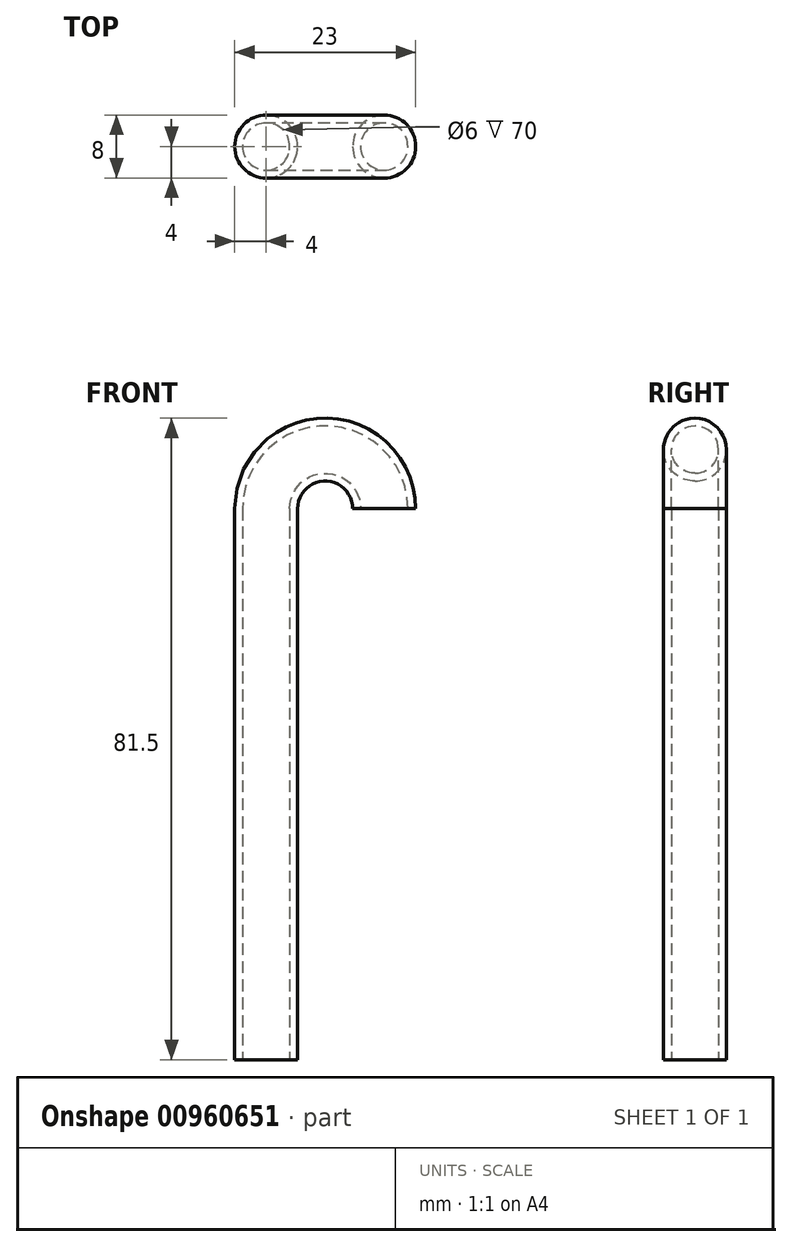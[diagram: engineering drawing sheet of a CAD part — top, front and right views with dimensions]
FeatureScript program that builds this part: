
annotation { "Feature Type Name" : "Feature", "Feature Type Description" : "" }
export const myFeature = defineFeature(function(context is Context, id is Id, definition is map)
    precondition{}
    {
        {
            var Q0;
            Q0=qCreatedBy(makeId("Top.planeOp"),FACE);
            var sketch = newSketch(context, id + "F0", { "sketchPlane" : qUnion([Q0])});
            skCircle(sketch, "E0", {"center": v(0, 0) * mm, "radius": 4 * mm});
            skCircle(sketch, "E1", {"center": v(0, 0) * mm, "radius": 3 * mm});
            skSolve(sketch);
        }
        {
            var Q0;
            Q0=makeQuery(id+"F0.imprint","IMPRINT",FACE,{"disambiguationData":[TD([[makeQuery(id+"F0.imprint","IMPRINT",EDGE,{"derivedFrom":sQuery(id+"F0.wireOp",EDGE,"E0")}),1.0]])]});
            extrude(context, id + "F1", {"entities" : qUnion([Q0]), "depth" : 70 * mm, "offsetDistance" : 25 * mm});
        }
        {
            var Q0;
            Q0=makeQuery(id+"F1.opExtrude","CAP_FACE",FACE,{"disambiguationData":[OSD([sQuery(id+"F0.wireOp",EDGE,"E0"),sQuery(id+"F0.wireOp",EDGE,"E1")])],"isStart":false});
            var sketch = newSketch(context, id + "F2", { "sketchPlane" : qUnion([Q0])});
            skCircle(sketch, "E2", {"center": v(0, 0) * mm, "radius": 4 * mm});
            skCircle(sketch, "E3", {"center": v(0, 0) * mm, "radius": 3 * mm});
            skSolve(sketch);
        }
        {
            var Q0;
            Q0=qCreatedBy(makeId("Front.planeOp"),FACE);
            var sketch = newSketch(context, id + "F3", { "sketchPlane" : qUnion([Q0])});
            skPoint(sketch, "E4", {"position": v(0, 70) * mm});
            skPoint(sketch, "E5", {"position": v(15, 70) * mm});
            skPoint(sketch, "E6", {"position": v(7.5, 77.5) * mm});
            skArc(sketch, "E7", {"start": v(15, 70) * mm, "mid": v(7.5, 77.5) * mm, "end": v(0, 70) * mm});
            skSolve(sketch);
        }
        {
            var Q0;
            Q0=makeQuery(id+"F2.imprint","IMPRINT",FACE,{"disambiguationData":[TD([[makeQuery(id+"F2.imprint","IMPRINT",EDGE,{"derivedFrom":sQuery(id+"F2.wireOp",EDGE,"E2")}),1.0]])]});
            var Q1;
            Q1=sQuery(id+"F3.wireOp",EDGE,"E7");
            sweep(context, id + "F4", {"operationType" : NewBodyOperationType.ADD, "profiles" : qUnion([Q0]), "path" : qUnion([Q1])});
        }
    });
